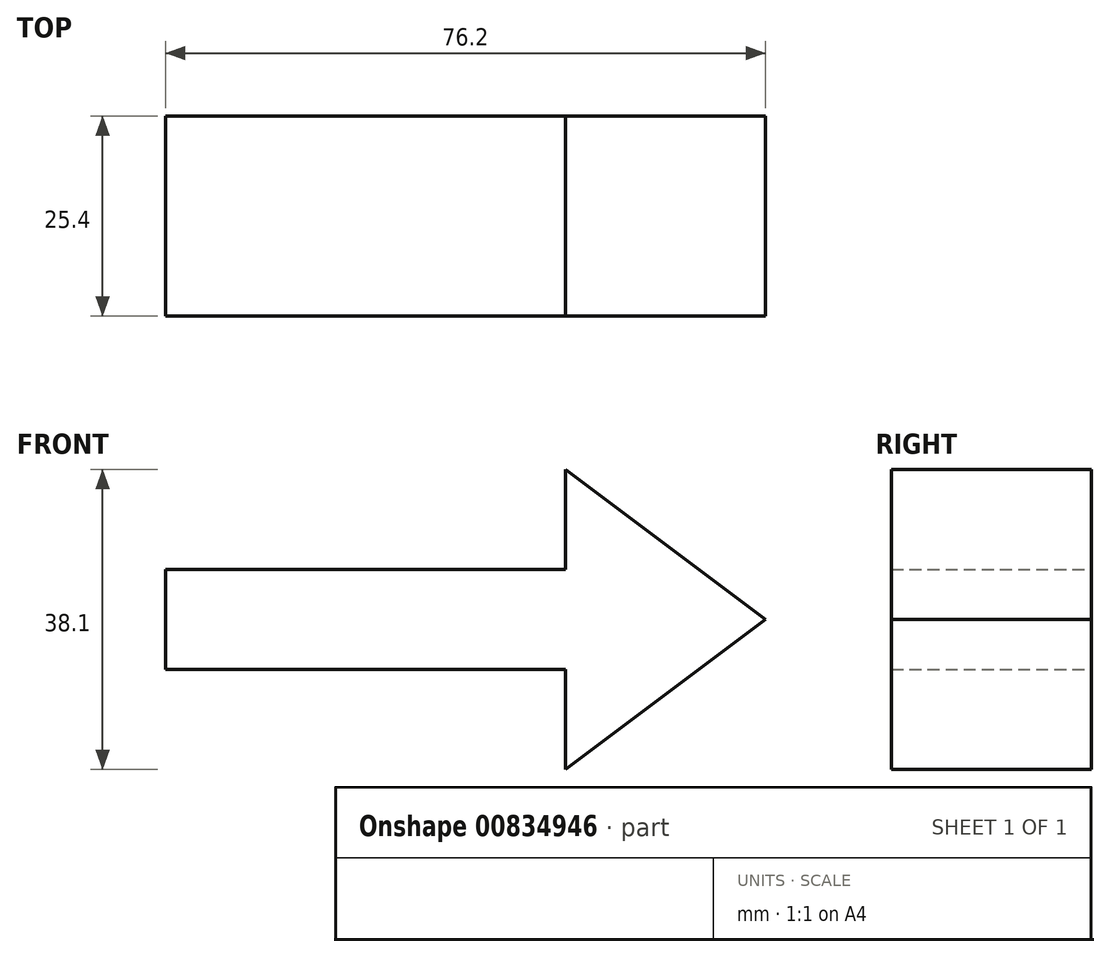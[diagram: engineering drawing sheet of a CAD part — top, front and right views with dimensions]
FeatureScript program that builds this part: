
annotation { "Feature Type Name" : "Feature", "Feature Type Description" : "" }
export const myFeature = defineFeature(function(context is Context, id is Id, definition is map)
    precondition{}
    {
        {
            var Q0;
            Q0=qCreatedBy(makeId("Front.planeOp"),FACE);
            var sketch = newSketch(context, id + "F0", { "sketchPlane" : qUnion([Q0])});
            skLineSegment(sketch, "E0", {"start": v(0, 6.35) * mm, "end": v(0, -6.35) * mm});
            skLineSegment(sketch, "E1", {"start": v(0, 6.35) * mm, "end": v(50.8, 6.35) * mm});
            skLineSegment(sketch, "E2", {"start": v(50.8, 6.35) * mm, "end": v(50.8, 19.05) * mm});
            skLineSegment(sketch, "E3", {"start": v(50.8, 19.05) * mm, "end": v(76.2, 0) * mm});
            skLineSegment(sketch, "E4", {"start": v(76.2, 0) * mm, "end": v(50.8, -19.05) * mm});
            skLineSegment(sketch, "E5", {"start": v(50.8, -19.05) * mm, "end": v(50.8, -6.35) * mm});
            skLineSegment(sketch, "E6", {"start": v(50.8, -6.35) * mm, "end": v(0, -6.35) * mm});
            skLineSegment(sketch, "E7", {"start": v(50.8, 6.35) * mm, "end": v(50.8, -6.35) * mm, "construction": true});
            skSolve(sketch);
        }
        {
            var Q0;
            Q0=makeQuery(id+"F0.imprint","IMPRINT",FACE,{"disambiguationData":[TD([[makeQuery(id+"F0.imprint","IMPRINT",EDGE,{"derivedFrom":sQuery(id+"F0.wireOp",EDGE,"E0")}),1.0]])]});
            extrude(context, id + "F1", {"entities" : qUnion([Q0]), "depth" : 25.4 * mm, "offsetDistance" : 25.4 * mm});
        }
    });
